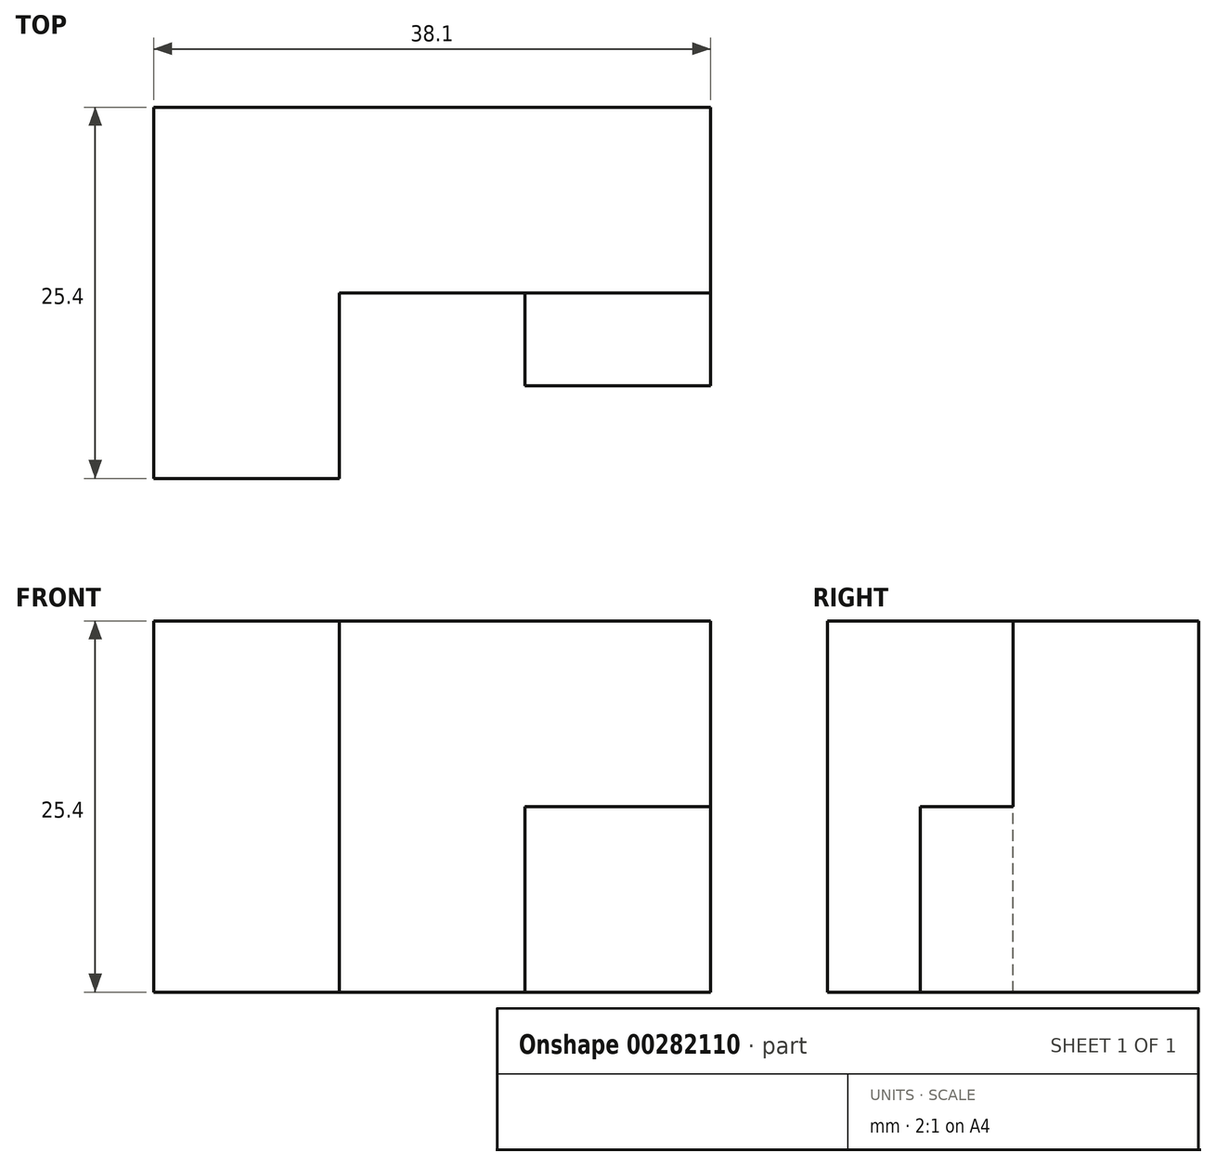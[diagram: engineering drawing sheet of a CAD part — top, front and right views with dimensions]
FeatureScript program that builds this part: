
annotation { "Feature Type Name" : "Feature", "Feature Type Description" : "" }
export const myFeature = defineFeature(function(context is Context, id is Id, definition is map)
    precondition{}
    {
        {
            var Q0;
            Q0=qCreatedBy(makeId("Top.planeOp"),FACE);
            var sketch = newSketch(context, id + "F0", { "sketchPlane" : qUnion([Q0])});
            skLineSegment(sketch, "E0", {"start": v(0, 0) * mm, "end": v(0, 25.4) * mm});
            skLineSegment(sketch, "E1", {"start": v(0, 25.4) * mm, "end": v(38.1, 25.4) * mm});
            skLineSegment(sketch, "E2", {"start": v(38.1, 25.4) * mm, "end": v(38.1, 12.7) * mm});
            skLineSegment(sketch, "E3", {"start": v(38.1, 12.7) * mm, "end": v(12.7, 12.7) * mm});
            skLineSegment(sketch, "E4", {"start": v(12.7, 12.7) * mm, "end": v(12.7, 0) * mm});
            skLineSegment(sketch, "E5", {"start": v(12.7, 0) * mm, "end": v(0, 0) * mm});
            skSolve(sketch);
        }
        {
            var Q0;
            Q0 = qSketchRegion(id + "F0", true);
            extrude(context, id + "F1", {"entities" : qUnion([Q0]), "depth" : 25.4 * mm});
        }
        {
            var Q0;
            Q0=makeQuery(id+"F1.opExtrude","SWEPT_FACE",FACE,{"disambiguationData":[OSD([sQuery(id+"F0.wireOp",EDGE,"E3")])]});
            var sketch = newSketch(context, id + "F2", { "sketchPlane" : qUnion([Q0])});
            skLineSegment(sketch, "E6", {"start": v(25.4, 0) * mm, "end": v(25.4, 12.7) * mm});
            skLineSegment(sketch, "E7", {"start": v(25.4, 12.7) * mm, "end": v(38.1, 12.7) * mm});
            skSolve(sketch);
        }
        {
            var Q0;
            Q0 = qSketchRegion(id + "F2", true);
            var Q1;
            {var subQ0=sQuery(id+"F2.wireOp",EDGE,"E6");Q1=makeQuery(id+"F2.imprint","IMPRINT",FACE,{"disambiguationData":[TD([[makeQuery(id+"F2.imprint","IMPRINT",EDGE,{"derivedFrom":subQ0}),-1.0]])]});}
            extrude(context, id + "F3", {"entities" : qUnion([Q0, Q1]), "operationType" : NewBodyOperationType.ADD, "depth" : 6.35 * mm});
        }
    });
